# Revit family: BIM_Model_Sanisett_Coronada_50_ 250_WTS
name_source: partatom
category: Mechanical Equipment
revit_build: Autodesk Revit 2018 (Build: 20170223_1515(x64)
units: mm (PartAtom-declared; Revit-internal decimal feet)

## family parameters
Always vertical = Yes
Cut with Voids When Loaded = No
Part Type = Normal
Room Calculation Point = No
Round Connector Dimension = Use Radius
Shared = No
Work Plane-Based = No

## types (1)
- Coronada 250 W/KS
    Cable = Neoprene
    Cable (HO7RN-F) = 3G 1.0
    Cable Length (m) = 10
    Capacity = 180 litres
    Description = The Sanisett 1 and 2 are single and twin pumping stations designed as a complete wastewater sump for above- or below-ground use. They provide effective dewatering of fecal-free domestic and commercial wastewater, from buildings and areas below the sewer level in accordance with EN 12050-2.
    Dimension A = 130 mm  [stored 0.426509 ft]
    Dimension B = 725 mm  [stored 2.37861 ft]
    Dimension C = 950 mm  [stored 3.1168 ft]
    Discharge DN 40 = 20 mm  [stored 0.0656168 ft]
    Discharge DN 50 = 25 mm  [stored 0.082021 ft]
    Impeller = PPO
    Inflow / Vent DN 70 = 35 mm  [stored 0.114829 ft]
    Inflow DN 100 = 50 mm  [stored 0.164042 ft]
    Inflow DN 100/150 = 50 mm  [stored 0.164042 ft]
    Manufacturer = Sulzer
    Model = Lifting Station Type ABS Sanisett 1 and 2
    Motor Power (kW) = P1=0.50 P2=0.25
    Motor housing = Stainless steel 1.4301 (AISI 304)
    Product Specification Link = http://www.sulzer.com
    Pump Discharge Internal Thread = G 1¼"
    Pump Weight = 4.5
    Pump housing = Stainless steel 1.4301 (AISI 304)
    Rated Current (A) = 2.28
    Rated Voltage (V) = 200-240 1~
    Rotor shaft = Stainless steel 1.4305 (AISI 303)
    Solids Passage (mm) = 10
    Speed (r/min) = 2900
    Tank Material = Polyethylene
    Weight (Kg) = 14kg (Without Pump)

note: [stored X ft] marks values corroborated as IEEE doubles in the binary element streams (Revit-internal decimal feet)

## geometry (parser evidence)
native form markers: Sweep x3
no freeform markers — native parametric forms only
